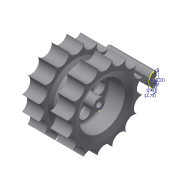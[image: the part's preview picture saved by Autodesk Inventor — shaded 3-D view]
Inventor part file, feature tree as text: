
AUTODESK INVENTOR PART (.ipt)
format: ipt  version: 2015 (Build 190159000, 159)  size: 294,912 bytes
history: native  units: mm
features: sketch x12, hole x4, revolve x1, extrude x1
ambient origin geometry x8: Origin, YZ Plane, XZ Plane, XY Plane, X Axis, Y Axis, Z Axis, Center Point
bodies: Solid1 (feature_tree)
feature tree (18):
  revolve  "Revolution1"  [1 undecoded]
  hole  "Hole1"  [1 undecoded]
  hole  "Hole2"  [1 undecoded]
  sketch  "Sketch4"  dims[d14=90.0deg d15=3.0mm]
  hole  "Hole3"  [1 undecoded]
  sketch  "Sketch6"  dims[d18=3.0mm]
  sketch  "Sketch7"  dims[d19=5.0mm d20=6.0mm d21=4.0mm d22=2.0mm d23=90.0deg d24=8.0mm d25=0.0mm d26=5.0mm]
  sketch  "Sketch8"  dims[d27=5.0mm]
  hole  "Hole4"  [1 undecoded]
  sketch  "Sketch9"  dims[d29=5.0mm]
  extrude  "Extrusion1"  Depth=5.0mm
  sketch  "Sketch11"  dims[d32=3.0mm]
  sketch  "Sketch12"  dims[d33=3.0mm d34=3.0mm d35=4.0mm d36=6.0mm d37=4.0mm d38=2.0mm d39=90.0deg d40=8.0mm d41=0.0mm d42=2.0mm d43=6.0mm d44=4.0mm d45=2.0mm d46=90.0deg d47=20.0mm d48=0.0mm d49=2.0mm d50=1.0mm d51=4.0mm d52=4.0mm d53=6.0mm d54=14.0mm d55=14.0mm d56=14.0mm d57=14.0mm d58=14.0mm d59=45.0deg d60=14.0mm d61=135.0deg d62=14.0mm d63=135.0deg d64=14.0mm d65=14.0mm d66=22.5deg d67=14.0mm d68=14.0mm d69=14.0mm d70=112.5deg d71=14.0mm d72=157.5deg d73=14.0mm d74=157.5deg d75=14.0mm d76=112.5deg d77=5.5mm d78=6.0mm d79=4.0mm d80=2.0mm d81=90.0deg d82=20.0mm d83=0.0mm d93=16.0mm d94=0.0mm d99=0.616266mm d102=1.902855mm d103=6.0mm d104=5.232531mm d105=2.75mm]
  sketch  "Sketch1"  dims[d0=6.0mm d1=2.0mm]
  sketch  "Sketch2"  dims[d3=5.0mm d6=12.0mm]
  sketch  "Sketch3"  dims[d7=2.0mm d8=5.0mm]
  sketch  "Sketch5"  dims[d16=3.0mm d17=3.0mm]
  sketch  "Sketch10"  dims[d31=3.0mm]
note: 5 required parameter values undecoded (feature->parameter linkage not recoverable at this tier; creation-order binding heuristic only, values carry confidence <= 0.55)